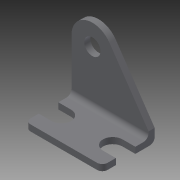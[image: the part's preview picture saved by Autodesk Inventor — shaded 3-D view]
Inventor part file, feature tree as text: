
AUTODESK INVENTOR PART (.ipt)
format: ipt  version: 2014 (Build 180170000, 170)  size: 194,560 bytes
history: native  units: in
note: dims shown in document units (in); Inventor stores cm internally (conversion verified against a paired STEP export)
features: other x161, sketch x8, extrude x5, hole x3
ambient origin geometry x8: Origin, YZ Plane, XZ Plane, XY Plane, X Axis, Y Axis, Z Axis, Center Point
bodies: Solid1 (feature_tree)
feature tree (177):
  extrude  "Extrusion1"  Depth=0.51in TaperAngle=0.0deg
  extrude  "Extrusion2"  Depth=0.0598in TaperAngle=0.0deg
  hole  "Hole1"  [1 undecoded]
  hole  "Hole2"  [1 undecoded]
  hole  "Hole3"  [1 undecoded]
  sketch  "Sketch_6"
  sketch  "Sketch_7"
  extrude  "Extrusion3"  [1 undecoded]
  extrude  "Extrusion4"  [1 undecoded]
  extrude  "Extrusion5"  [1 undecoded]
  other  "a1_XY"
  other  "a1_YZ"
  other  "a1_ZX"
  other  "a1_X"
  other  "a1_Y"
  other  "a1_Z"
  other  "a1_Center"
  other  "a2_XY"
  other  "a2_YZ"
  other  "a2_ZX"
  other  "a2_X"
  other  "a2_Y"
  other  "a2_Z"
  other  "a2_Center"
  other  "b1_XY"
  other  "b1_YZ"
  other  "b1_ZX"
  other  "b1_X"
  other  "b1_Y"
  other  "b1_Z"
  other  "b1_Center"
  other  "b2_XY"
  other  "b2_YZ"
  other  "b2_ZX"
  other  "b2_X"
  other  "b2_Y"
  other  "b2_Z"
  other  "b2_Center"
  other  "c1_XY"
  other  "c1_YZ"
  other  "c1_ZX"
  other  "c1_X"
  other  "c1_Y"
  other  "c1_Z"
  other  "c1_Center"
  other  "d1_XY"
  other  "d1_YZ"
  other  "d1_ZX"
  other  "d1_X"
  other  "d1_Y"
  other  "d1_Z"
  other  "d1_Center"
  other  "d2_XY"
  other  "d2_YZ"
  other  "d2_ZX"
  other  "d2_X"
  other  "d2_Y"
  other  "d2_Z"
  other  "d2_Center"
  other  "e1_XY"
  other  "e1_YZ"
  other  "e1_ZX"
  other  "e1_X"
  other  "e1_Y"
  other  "e1_Z"
  other  "e1_Center"
  other  "e2_XY"
  other  "e2_YZ"
  other  "e2_ZX"
  other  "e2_X"
  other  "e2_Y"
  other  "e2_Z"
  other  "e2_Center"
  other  "f1_XY"
  other  "f1_YZ"
  other  "f1_ZX"
  other  "f1_X"
  other  "f1_Y"
  other  "f1_Z"
  other  "f1_Center"
  other  "f2_XY"
  other  "f2_YZ"
  other  "f2_ZX"
  other  "f2_X"
  other  "f2_Y"
  other  "f2_Z"
  other  "f2_Center"
  other  "g1_XY"
  other  "g1_YZ"
  other  "g1_ZX"
  other  "g1_X"
  other  "g1_Y"
  other  "g1_Z"
  other  "g1_Center"
  other  "g2_XY"
  other  "g2_YZ"
  other  "g2_ZX"
  other  "g2_X"
  other  "g2_Y"
  other  "g2_Z"
  other  "g2_Center"
  other  "h1_XY"
  other  "h1_YZ"
  other  "h1_ZX"
  other  "h1_X"
  other  "h1_Y"
  other  "h1_Z"
  other  "h1_Center"
  other  "h2_XY"
  other  "h2_YZ"
  other  "h2_ZX"
  other  "h2_X"
  other  "h2_Y"
  other  "h2_Z"
  other  "h2_Center"
  other  "i_XY"
  other  "i_YZ"
  other  "i_ZX"
  other  "i_X"
  other  "i_Y"
  other  "i_Z"
  other  "i_Center"
  other  "j1_XY"
  other  "j1_YZ"
  other  "j1_ZX"
  other  "j1_X"
  other  "j1_Y"
  other  "j1_Z"
  other  "j1_Center"
  other  "j2_XY"
  other  "j2_YZ"
  other  "j2_ZX"
  other  "j2_X"
  other  "j2_Y"
  other  "j2_Z"
  other  "j2_Center"
  other  "k1_XY"
  other  "k1_YZ"
  other  "k1_ZX"
  other  "k1_X"
  other  "k1_Y"
  other  "k1_Z"
  other  "k1_Center"
  other  "k11_XY"
  other  "k11_YZ"
  other  "k11_ZX"
  other  "k11_X"
  other  "k11_Y"
  other  "k11_Z"
  other  "k11_Center"
  other  "k12_XY"
  other  "k12_YZ"
  other  "k12_ZX"
  other  "k12_X"
  other  "k12_Y"
  other  "k12_Z"
  other  "k12_Center"
  other  "to_dummy_L_XY"
  other  "to_dummy_L_YZ"
  other  "to_dummy_L_ZX"
  other  "to_dummy_L_X"
  other  "to_dummy_L_Y"
  other  "to_dummy_L_Z"
  other  "to_dummy_L_Center"
  other  "to_pin_L_XY"
  other  "to_pin_L_YZ"
  other  "to_pin_L_ZX"
  other  "to_pin_L_X"
  other  "to_pin_L_Y"
  other  "to_pin_L_Z"
  other  "to_pin_L_Center"
  sketch  "Sketch_1"  dims[d0=0.75in d1=0.0in d2=0.51in d3=0.0in]
  sketch  "Sketch_2"  dims[d4=0.1585in d5=0.75in d6=0.375in d7=0.25in d8=0.5635in d9=0.0598in d10=0.0in]
  sketch  "Sketch3"  dims[d11=0.19in d12=0.75in d13=0.375in d14=0.25in d15=0.5635in d16=0.0598in d17=0.0in]
  sketch  "Sketch4"  dims[d18=0.19in d19=0.75in d20=0.375in d21=0.25in d22=0.5635in d23=0.0598in d24=0.0in d25=0.0598in d26=0.0in]
  sketch  "Sketch5"  dims[d27=0.0598in d28=0.0in d29=0.0598in d30=0.0in]
  sketch  "Sketch_8"
note: 6 required parameter values undecoded (feature->parameter linkage not recoverable at this tier; creation-order binding heuristic only, values carry confidence <= 0.55)
